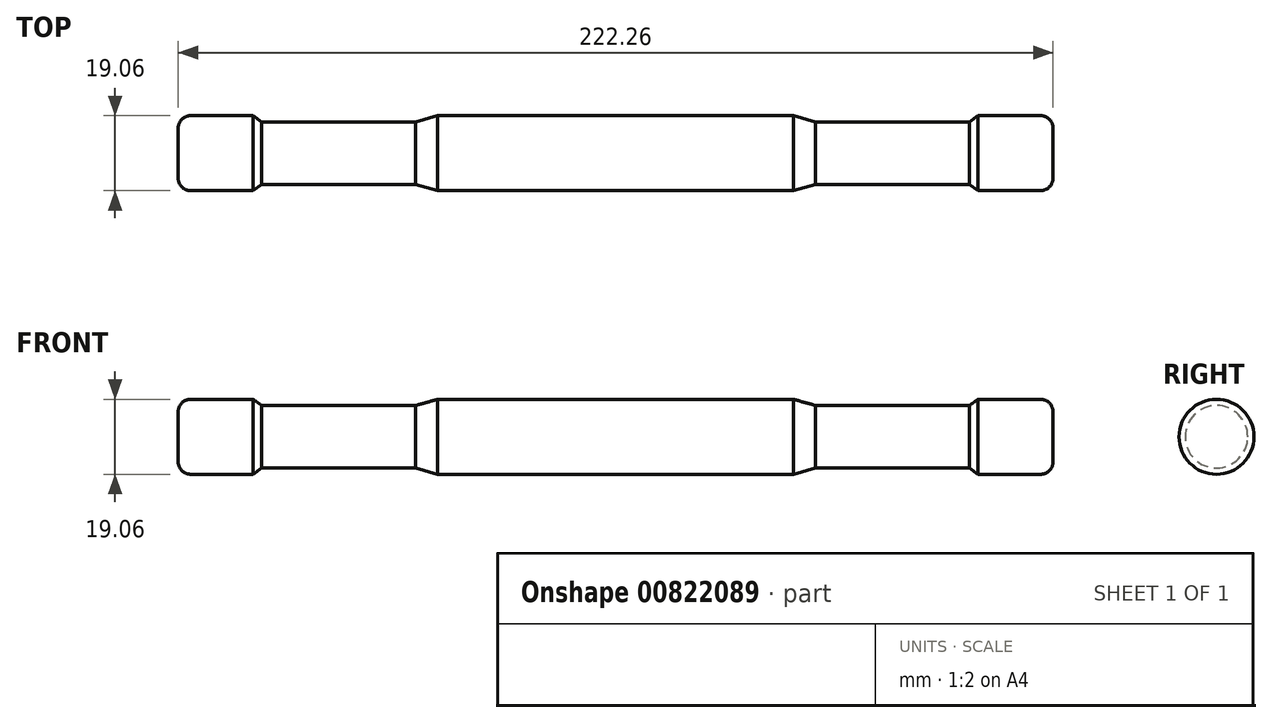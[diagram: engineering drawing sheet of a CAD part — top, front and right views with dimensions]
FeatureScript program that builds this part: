
annotation { "Feature Type Name" : "Feature", "Feature Type Description" : "" }
export const myFeature = defineFeature(function(context is Context, id is Id, definition is map)
    precondition{}
    {
        {
            var Q0;
            Q0=qCreatedBy(makeId("Front.planeOp"),FACE);
            var sketch = newSketch(context, id + "F0", { "sketchPlane" : qUnion([Q0])});
            skLineSegment(sketch, "E0.bottom", {"start": v(107.95, -9.52) * mm, "end": v(92.07, -9.52) * mm});
            skLineSegment(sketch, "E0.left", {"start": v(111.13, -6.35) * mm, "end": v(111.13, 0) * mm});
            skLineSegment(sketch, "E0.right", {"start": v(-111.13, -6.35) * mm, "end": v(-111.13, 0) * mm});
            skPoint(sketch, "E0.middle", {"position": v(0, 0) * mm});
            skLineSegment(sketch, "E1", {"start": v(-111.13, 0) * mm, "end": v(111.13, 0) * mm});
            skPoint(sketch, "E2.orphan", {"position": v(111.13, 9.53) * mm});
            skLineSegment(sketch, "E3", {"start": v(-50.8, -7.94) * mm, "end": v(-89.9, -7.94) * mm});
            skLineSegment(sketch, "E4", {"start": v(-92.07, -9.53) * mm, "end": v(-89.9, -7.94) * mm});
            skLineSegment(sketch, "E5", {"start": v(-50.8, -7.94) * mm, "end": v(-45.2, -9.53) * mm});
            skLineSegment(sketch, "E6.trimOffspring", {"start": v(-92.07, -9.53) * mm, "end": v(-107.95, -9.53) * mm});
            skLineSegment(sketch, "E7.MirrorCS", {"start": v(92.07, -9.53) * mm, "end": v(89.9, -7.94) * mm});
            skLineSegment(sketch, "E8.MirrorCS", {"start": v(50.8, -7.94) * mm, "end": v(45.2, -9.53) * mm});
            skLineSegment(sketch, "E9.MirrorCS", {"start": v(50.8, -7.94) * mm, "end": v(89.9, -7.94) * mm});
            skLineSegment(sketch, "E10.trimOffspring", {"start": v(45.2, -9.53) * mm, "end": v(-45.2, -9.53) * mm});
            skPoint(sketch, "E11.visualSharp", {"position": v(-111.13, -9.53) * mm});
            skArc(sketch, "E11.filletArc", {"start": v(-111.13, -6.35) * mm, "mid": v(-110.2, -8.6) * mm, "end": v(-107.95, -9.53) * mm});
            skPoint(sketch, "E12.visualSharp", {"position": v(111.13, -9.52) * mm});
            skArc(sketch, "E12.filletArc", {"start": v(107.95, -9.52) * mm, "mid": v(110.2, -8.6) * mm, "end": v(111.13, -6.35) * mm});
            skSolve(sketch);
        }
        {
            var Q0;
            {var subQ1=sQuery(id+"F0.wireOp",EDGE,"E0.bottom");Q0=makeQuery(id+"F0.imprint","IMPRINT",FACE,{"disambiguationData":[TD([[makeQuery(id+"F0.imprint","IMPRINT",EDGE,{"derivedFrom":subQ1}),-1.0]])]});}
            var Q1;
            Q1=sQuery(id+"F0.wireOp",EDGE,"E1");
            revolve(context, id + "F1", {"surfaceOperationType" : NewSurfaceOperationType.NEW, "entities" : qUnion([Q0]), "axis" : qUnion([Q1]), "revolveType" : RevolveType.FULL});
        }
    });
